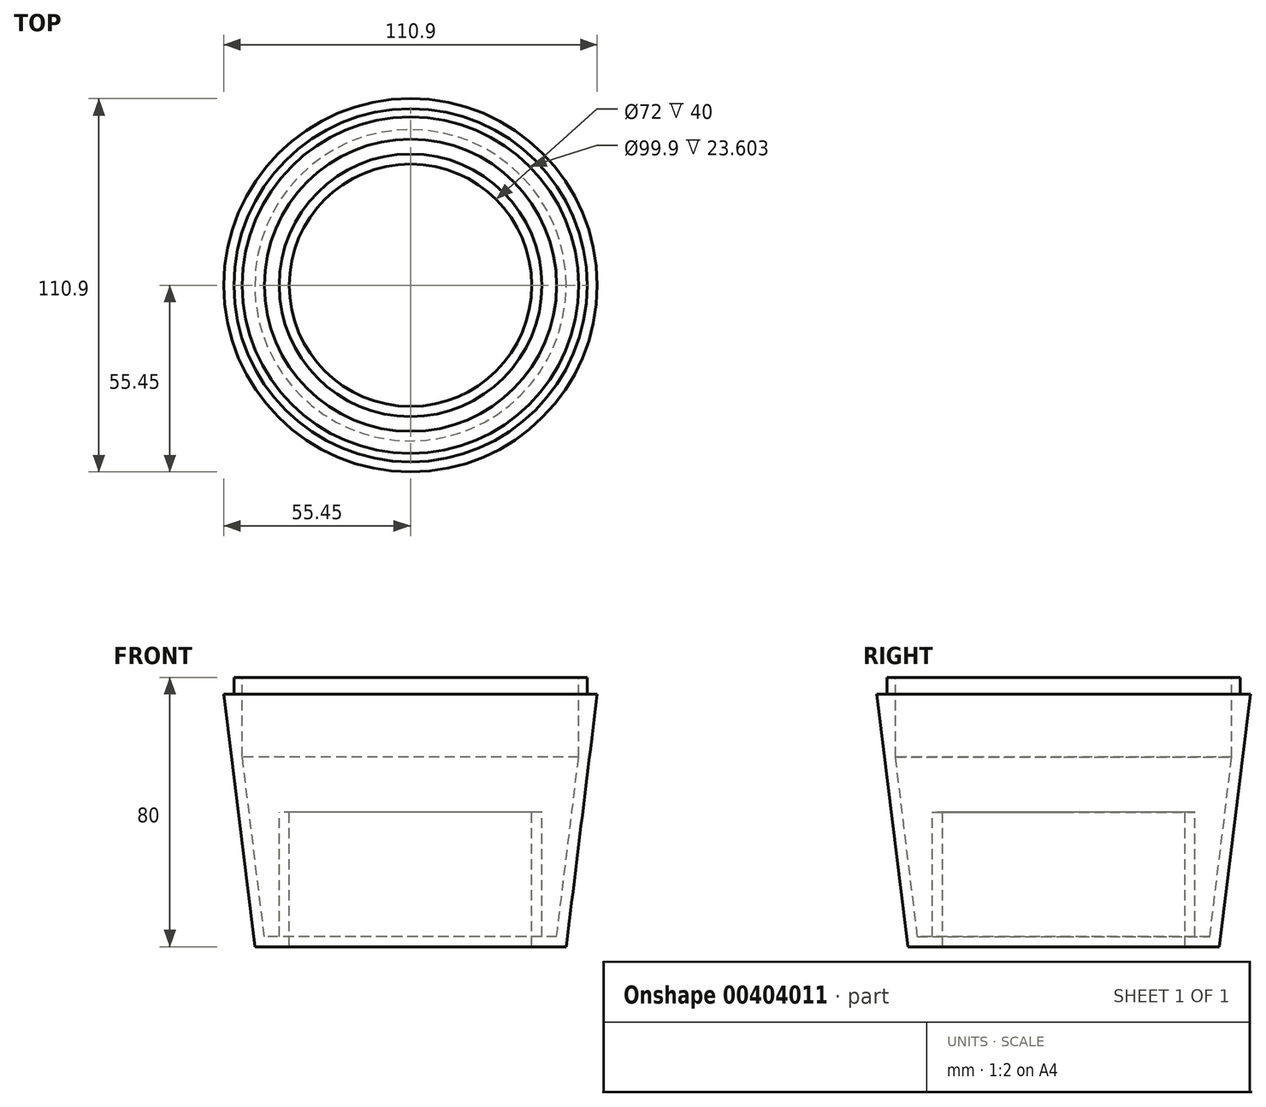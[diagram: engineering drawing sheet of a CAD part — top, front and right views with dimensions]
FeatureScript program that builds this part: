
annotation { "Feature Type Name" : "Feature", "Feature Type Description" : "" }
export const myFeature = defineFeature(function(context is Context, id is Id, definition is map)
    precondition{}
    {
        {
            var Q0;
            Q0=qCreatedBy(makeId("Front.planeOp"),FACE);
            var sketch = newSketch(context, id + "F0", { "sketchPlane" : qUnion([Q0])});
            skLineSegment(sketch, "E0", {"start": v(-55.45, 75) * mm, "end": v(-46.24, 0) * mm});
            skLineSegment(sketch, "E1", {"start": v(-46.24, 0) * mm, "end": v(-36, 0) * mm});
            skLineSegment(sketch, "E2", {"start": v(-36, 0) * mm, "end": v(-36, 40) * mm});
            skLineSegment(sketch, "E3", {"start": v(-36, 40) * mm, "end": v(-39, 40) * mm});
            skLineSegment(sketch, "E4", {"start": v(-39, 40) * mm, "end": v(-39, 3) * mm});
            skLineSegment(sketch, "E5", {"start": v(-39, 3) * mm, "end": v(-43.4, 3) * mm});
            skLineSegment(sketch, "E6", {"start": v(-43.4, 3) * mm, "end": v(-49.95, 56.4) * mm});
            skLineSegment(sketch, "E7", {"start": v(-52.45, 75) * mm, "end": v(-55.45, 75) * mm});
            skLineSegment(sketch, "E8", {"start": v(-52.45, 75) * mm, "end": v(-52.45, 75) * mm});
            skLineSegment(sketch, "E9", {"start": v(-52.45, 80) * mm, "end": v(-49.95, 80) * mm});
            skLineSegment(sketch, "E10", {"start": v(-49.95, 80) * mm, "end": v(-49.95, 56.4) * mm});
            skLineSegment(sketch, "E11", {"start": v(-49.95, 56.4) * mm, "end": v(-49.95, 56.4) * mm});
            skLineSegment(sketch, "E12", {"start": v(-52.45, 75) * mm, "end": v(-52.45, 80) * mm});
            skSolve(sketch);
        }
        {
            var Q0;
            Q0=qCreatedBy(makeId("Front.planeOp"),FACE);
            var sketch = newSketch(context, id + "F1", { "sketchPlane" : qUnion([Q0])});
            skLineSegment(sketch, "E13", {"start": v(0, 28.83) * mm, "end": v(0, -49.57) * mm});
            skSolve(sketch);
        }
        {
            var Q0;
            Q0 = qSketchRegion(id + "F1", true);
            var Q1;
            Q1=makeQuery(id+"F0.imprint","IMPRINT",FACE,{"disambiguationData":[TD([[makeQuery(id+"F0.imprint","IMPRINT",EDGE,{"derivedFrom":sQuery(id+"F0.wireOp",EDGE,"E0")}),1.0]])]});
            var Q2;
            Q2=sQuery(id+"F1.wireOp",EDGE,"E13");
            revolve(context, id + "F2", {"entities" : qUnion([Q0, Q1]), "axis" : qUnion([Q2]), "revolveType" : RevolveType.FULL});
        }
    });
